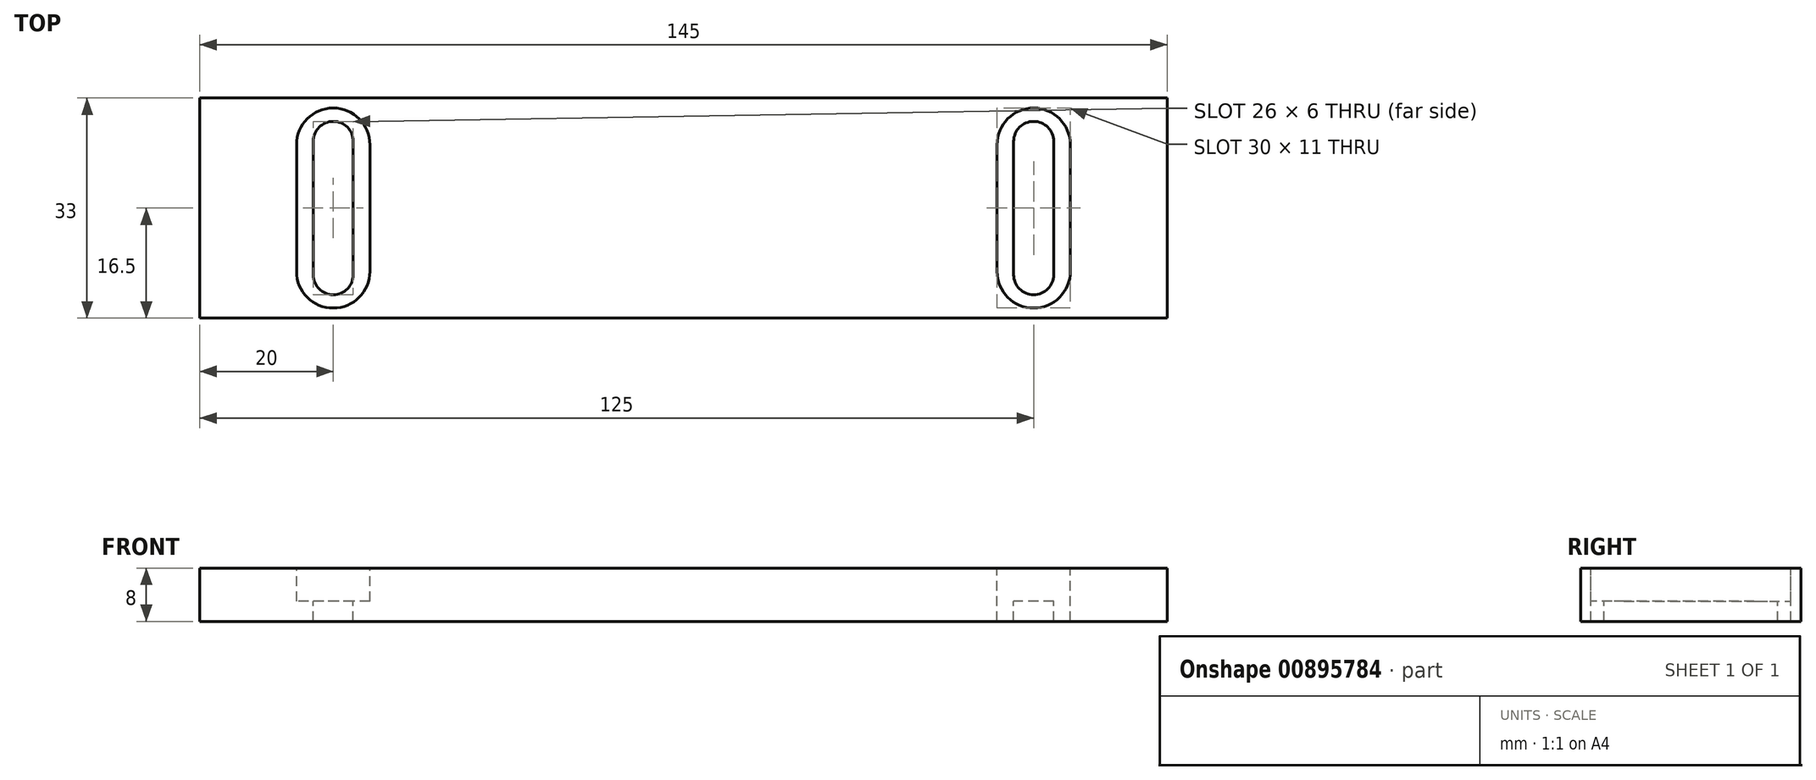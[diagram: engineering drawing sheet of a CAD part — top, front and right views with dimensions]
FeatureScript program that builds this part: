
annotation { "Feature Type Name" : "Feature", "Feature Type Description" : "" }
export const myFeature = defineFeature(function(context is Context, id is Id, definition is map)
    precondition{}
    {
        {
            var Q0;
            Q0=qCreatedBy(makeId("Top.planeOp"),FACE);
            var sketch = newSketch(context, id + "F0", { "sketchPlane" : qUnion([Q0])});
            skLineSegment(sketch, "E0.bottom", {"start": v(-72.5, 16.5) * mm, "end": v(72.5, 16.5) * mm});
            skLineSegment(sketch, "E0.top", {"start": v(-72.5, -16.5) * mm, "end": v(72.5, -16.5) * mm});
            skLineSegment(sketch, "E0.left", {"start": v(-72.5, 16.5) * mm, "end": v(-72.5, -16.5) * mm});
            skLineSegment(sketch, "E0.right", {"start": v(72.5, 16.5) * mm, "end": v(72.5, -16.5) * mm});
            skPoint(sketch, "E0.middle", {"position": v(0, 0) * mm});
            skLineSegment(sketch, "E1.bottom", {"start": v(-52.5, 13) * mm, "end": v(-52.5, 13) * mm});
            skLineSegment(sketch, "E1.top", {"start": v(-52.5, -13) * mm, "end": v(-52.5, -13) * mm});
            skLineSegment(sketch, "E1.left", {"start": v(-49.5, 10) * mm, "end": v(-49.5, -10) * mm});
            skLineSegment(sketch, "E1.right", {"start": v(-55.5, 10) * mm, "end": v(-55.5, -10) * mm});
            skPoint(sketch, "E1.middle", {"position": v(-52.5, 0) * mm});
            skPoint(sketch, "E2.visualSharp", {"position": v(-55.5, 13) * mm});
            skArc(sketch, "E2.filletArc", {"start": v(-52.5, 13) * mm, "mid": v(-54.62, 12.12) * mm, "end": v(-55.5, 10) * mm});
            skPoint(sketch, "E3.visualSharp", {"position": v(-49.5, 13) * mm});
            skArc(sketch, "E3.filletArc", {"start": v(-49.5, 10) * mm, "mid": v(-50.38, 12.12) * mm, "end": v(-52.5, 13) * mm});
            skPoint(sketch, "E4.visualSharp", {"position": v(-49.5, -13) * mm});
            skArc(sketch, "E4.filletArc", {"start": v(-52.5, -13) * mm, "mid": v(-50.38, -12.12) * mm, "end": v(-49.5, -10) * mm});
            skPoint(sketch, "E5.visualSharp", {"position": v(-55.5, -13) * mm});
            skArc(sketch, "E5.filletArc", {"start": v(-55.5, -10) * mm, "mid": v(-54.62, -12.12) * mm, "end": v(-52.5, -13) * mm});
            skLineSegment(sketch, "E6.bottom", {"start": v(-52.5, 15) * mm, "end": v(-52.5, 15) * mm});
            skLineSegment(sketch, "E6.top", {"start": v(-52.5, -15) * mm, "end": v(-52.5, -15) * mm});
            skLineSegment(sketch, "E6.left", {"start": v(-58, 9.5) * mm, "end": v(-58, -9.5) * mm});
            skLineSegment(sketch, "E6.right", {"start": v(-47, 9.5) * mm, "end": v(-47, -9.5) * mm});
            skPoint(sketch, "E7.visualSharp", {"position": v(-58, 15) * mm});
            skArc(sketch, "E7.filletArc", {"start": v(-52.5, 15) * mm, "mid": v(-56.39, 13.39) * mm, "end": v(-58, 9.5) * mm});
            skPoint(sketch, "E8.visualSharp", {"position": v(-47, 15) * mm});
            skArc(sketch, "E8.filletArc", {"start": v(-47, 9.5) * mm, "mid": v(-48.61, 13.39) * mm, "end": v(-52.5, 15) * mm});
            skPoint(sketch, "E9.visualSharp", {"position": v(-47, -15) * mm});
            skArc(sketch, "E9.filletArc", {"start": v(-52.5, -15) * mm, "mid": v(-48.61, -13.39) * mm, "end": v(-47, -9.5) * mm});
            skPoint(sketch, "E10.visualSharp", {"position": v(-58, -15) * mm});
            skArc(sketch, "E10.filletArc", {"start": v(-58, -9.5) * mm, "mid": v(-56.39, -13.39) * mm, "end": v(-52.5, -15) * mm});
            skArc(sketch, "E11.MirrorCS", {"start": v(49.5, 10) * mm, "mid": v(50.38, 12.12) * mm, "end": v(52.5, 13) * mm});
            skArc(sketch, "E12.MirrorCS", {"start": v(52.5, -13) * mm, "mid": v(50.38, -12.12) * mm, "end": v(49.5, -10) * mm});
            skArc(sketch, "E13.MirrorCS", {"start": v(47, 9.5) * mm, "mid": v(48.61, 13.39) * mm, "end": v(52.5, 15) * mm});
            skArc(sketch, "E14.MirrorCS", {"start": v(55.5, -10) * mm, "mid": v(54.62, -12.12) * mm, "end": v(52.5, -13) * mm});
            skArc(sketch, "E15.MirrorCS", {"start": v(52.5, -15) * mm, "mid": v(48.61, -13.39) * mm, "end": v(47, -9.5) * mm});
            skArc(sketch, "E16.MirrorCS", {"start": v(58, -9.5) * mm, "mid": v(56.39, -13.39) * mm, "end": v(52.5, -15) * mm});
            skArc(sketch, "E17.MirrorCS", {"start": v(52.5, 13) * mm, "mid": v(54.62, 12.12) * mm, "end": v(55.5, 10) * mm});
            skPoint(sketch, "E18.MirrorP", {"position": v(52.5, 0) * mm});
            skArc(sketch, "E19.MirrorCS", {"start": v(52.5, 15) * mm, "mid": v(56.39, 13.39) * mm, "end": v(58, 9.5) * mm});
            skPoint(sketch, "E20.MirrorP", {"position": v(47, -15) * mm});
            skLineSegment(sketch, "E21.MirrorCS", {"start": v(47, 9.5) * mm, "end": v(47, -9.5) * mm});
            skLineSegment(sketch, "E22.MirrorCS", {"start": v(58, 9.5) * mm, "end": v(58, -9.5) * mm});
            skPoint(sketch, "E23.MirrorP", {"position": v(49.5, -13) * mm});
            skLineSegment(sketch, "E24.MirrorCS", {"start": v(52.5, -13) * mm, "end": v(52.5, -13) * mm});
            skPoint(sketch, "E25.MirrorP", {"position": v(47, 15) * mm});
            skPoint(sketch, "E26.MirrorP", {"position": v(58, 15) * mm});
            skLineSegment(sketch, "E27.MirrorCS", {"start": v(52.5, 15) * mm, "end": v(52.5, 15) * mm});
            skPoint(sketch, "E28.MirrorP", {"position": v(55.5, -13) * mm});
            skPoint(sketch, "E29.MirrorP", {"position": v(55.5, 13) * mm});
            skLineSegment(sketch, "E30.MirrorCS", {"start": v(49.5, 10) * mm, "end": v(49.5, -10) * mm});
            skLineSegment(sketch, "E31.MirrorCS", {"start": v(55.5, 10) * mm, "end": v(55.5, -10) * mm});
            skLineSegment(sketch, "E32.MirrorCS", {"start": v(52.5, -15) * mm, "end": v(52.5, -15) * mm});
            skPoint(sketch, "E33.MirrorP", {"position": v(58, -15) * mm});
            skPoint(sketch, "E34.MirrorP", {"position": v(49.5, 13) * mm});
            skLineSegment(sketch, "E35.MirrorCS", {"start": v(52.5, 13) * mm, "end": v(52.5, 13) * mm});
            skPoint(sketch, "E36.right.end.orphan", {"position": v(0, -16.5) * mm});
            skPoint(sketch, "E36.left.end.orphan", {"position": v(-40, 16.5) * mm});
            skPoint(sketch, "E36.left.start.orphan", {"position": v(-40, 0) * mm});
            skPoint(sketch, "E37.MirrorCS.start.orphan", {"position": v(40, 0) * mm});
            skPoint(sketch, "E38.MirrorCS.end.orphan", {"position": v(40, 16.5) * mm});
            skSolve(sketch);
        }
        {
            var Q0;
            Q0=makeQuery(id+"F0.imprint","IMPRINT",FACE,{"disambiguationData":[TD([[makeQuery(id+"F0.imprint","IMPRINT",EDGE,{"derivedFrom":sQuery(id+"F0.wireOp",EDGE,"E0.bottom")}),-1.0]])]});
            var Q1;
            Q1=makeQuery(id+"F0.imprint","IMPRINT",FACE,{"disambiguationData":[TD([[makeQuery(id+"F0.imprint","IMPRINT",EDGE,{"derivedFrom":sQuery(id+"F0.wireOp",EDGE,"E1.left")}),1.0]])]});
            var Q2;
            Q2=makeQuery(id+"F0.imprint","IMPRINT",FACE,{"disambiguationData":[TD([[makeQuery(id+"F0.imprint","IMPRINT",EDGE,{"derivedFrom":sQuery(id+"F0.wireOp",EDGE,"E11.MirrorCS")}),1.0]])]});
            extrude(context, id + "F1", {"entities" : qUnion([Q0, Q1, Q2]), "oppositeDirection" : true, "depth" : 8 * mm, "offsetDistance" : 25 * mm});
        }
        {
            var Q0;
            Q0=makeQuery(id+"F0.imprint","IMPRINT",FACE,{"disambiguationData":[TD([[makeQuery(id+"F0.imprint","IMPRINT",EDGE,{"derivedFrom":sQuery(id+"F0.wireOp",EDGE,"E1.left")}),-1.0]])]});
            var Q1;
            Q1=makeQuery(id+"F0.imprint","IMPRINT",FACE,{"disambiguationData":[TD([[makeQuery(id+"F0.imprint","IMPRINT",EDGE,{"derivedFrom":sQuery(id+"F0.wireOp",EDGE,"E11.MirrorCS")}),-1.0]])]});
            var Q2;
            Q2=makeQuery(id+"F0.imprint","IMPRINT",FACE,{"disambiguationData":[TD([[makeQuery(id+"F0.imprint","IMPRINT",EDGE,{"derivedFrom":sQuery(id+"F0.wireOp",EDGE,"E11.MirrorCS")}),1.0]])]});
            var Q3;
            Q3=makeQuery(id+"F0.imprint","IMPRINT",FACE,{"disambiguationData":[TD([[makeQuery(id+"F0.imprint","IMPRINT",EDGE,{"derivedFrom":sQuery(id+"F0.wireOp",EDGE,"E1.left")}),1.0]])]});
            extrude(context, id + "F2", {"entities" : qUnion([Q0, Q1, Q2, Q3]), "operationType" : NewBodyOperationType.REMOVE, "oppositeDirection" : true, "depth" : 5 * mm, "offsetDistance" : 25 * mm});
        }
    });
